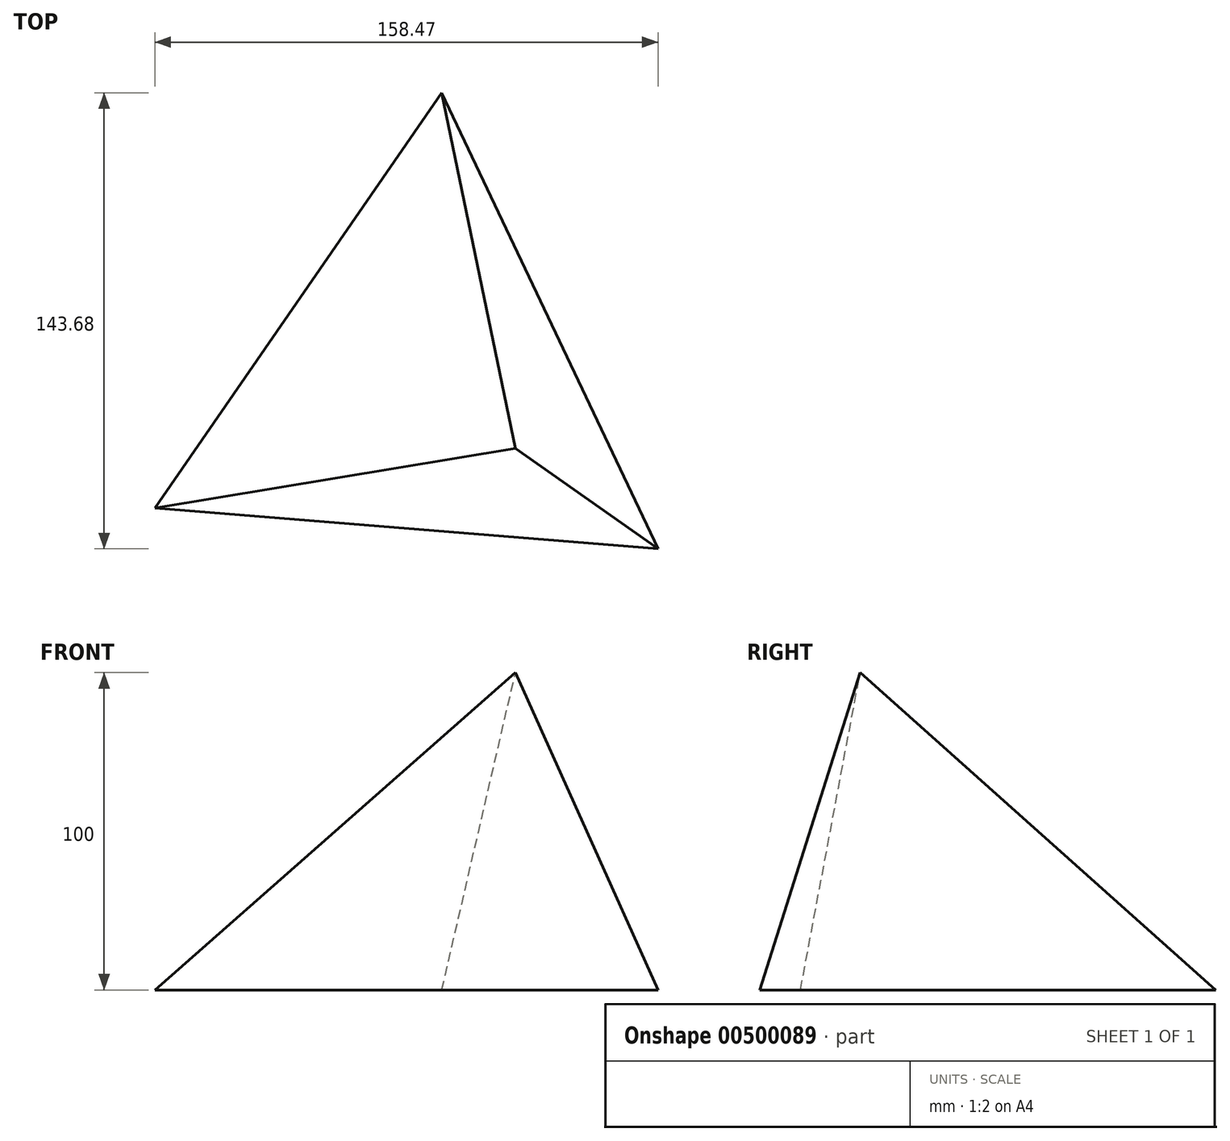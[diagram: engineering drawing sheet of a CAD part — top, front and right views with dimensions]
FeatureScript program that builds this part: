
annotation { "Feature Type Name" : "Feature", "Feature Type Description" : "" }
export const myFeature = defineFeature(function(context is Context, id is Id, definition is map)
    precondition{}
    {
        {
            var Q0;
            Q0=qCreatedBy(makeId("Top.planeOp"),FACE);
            var sketch = newSketch(context, id + "F0", { "sketchPlane" : qUnion([Q0])});
            skCircle(sketch, "E0.cCircle", {"center": v(-30.64, 20.5) * mm, "radius": 91.8 * mm, "construction": true});
            skLineSegment(sketch, "E0.0", {"start": v(44.9, -31.68) * mm, "end": v(-113.58, -18.82) * mm});
            skLineSegment(sketch, "E0.1", {"start": v(-113.58, -18.82) * mm, "end": v(-23.21, 112) * mm});
            skLineSegment(sketch, "E0.2", {"start": v(-23.21, 112) * mm, "end": v(44.9, -31.68) * mm});
            skSolve(sketch);
        }
        {
            var Q0;
            Q0=qCreatedBy(makeId("Top.planeOp"),FACE);
            cPlane(context, id + "F1", {"entities" : qUnion([Q0]), "cplaneType" : CPlaneType.OFFSET, "offset" : 100 * mm, "width" : 152.4 * mm, "height" : 152.4 * mm});
        }
        {
            var Q0;
            Q0=qCreatedBy(id+"F1.planeOp",FACE);
            var sketch = newSketch(context, id + "F2", { "sketchPlane" : qUnion([Q0])});
            skPoint(sketch, "E1", {"position": v(0, 0) * mm});
            skPoint(sketch, "E2", {"position": v(4.82, 0) * mm});
            skSolve(sketch);
        }
        {
            var Q0;
            Q0=makeQuery(id+"F0.imprint","IMPRINT",FACE,{"disambiguationData":[TD([[makeQuery(id+"F0.imprint","IMPRINT",EDGE,{"derivedFrom":sQuery(id+"F0.wireOp",EDGE,"E0.0")}),-1.0]])]});
            var Q1;
            Q1=sQuery(id+"F2.wireOp",VERTEX,"E1");
            loft(context, id + "F3", {"sheetProfilesArray" : [{ "sheetProfileEntities" : qUnion([Q0]) }, { "sheetProfileEntities" : qUnion([Q1]) }]});
        }
    });
